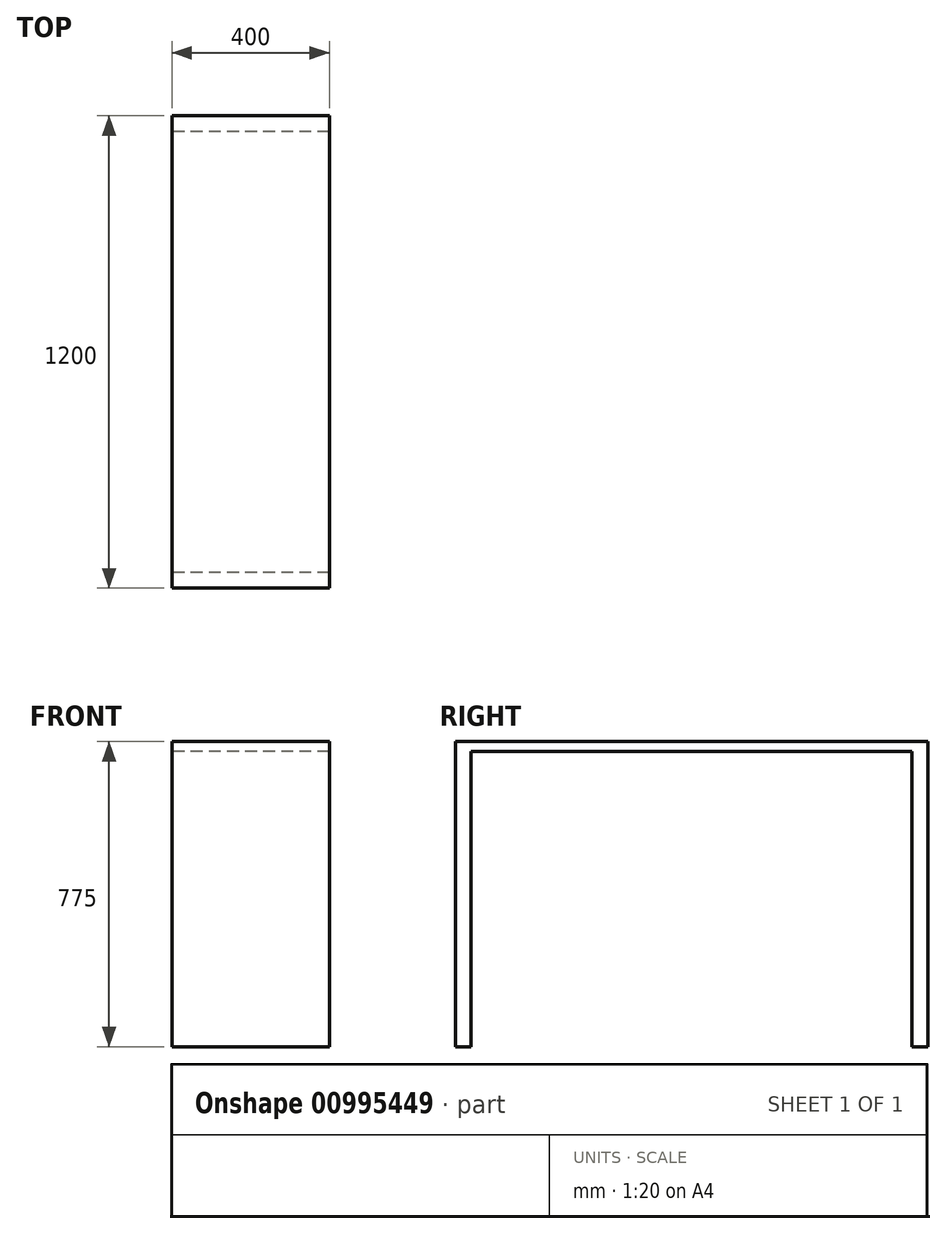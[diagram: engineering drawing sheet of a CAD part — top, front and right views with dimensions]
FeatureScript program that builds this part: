
annotation { "Feature Type Name" : "Feature", "Feature Type Description" : "" }
export const myFeature = defineFeature(function(context is Context, id is Id, definition is map)
    precondition{}
    {
        {
            var Q0;
            Q0=qCreatedBy(makeId("Top.planeOp"),FACE);
            var sketch = newSketch(context, id + "F0", { "sketchPlane" : qUnion([Q0])});
            skLineSegment(sketch, "E0.bottom", {"start": v(-183.76, 1047.63) * mm, "end": v(216.24, 1047.63) * mm});
            skLineSegment(sketch, "E0.top", {"start": v(-183.76, -152.37) * mm, "end": v(216.24, -152.37) * mm});
            skLineSegment(sketch, "E0.left", {"start": v(-183.76, 1047.63) * mm, "end": v(-183.76, -152.37) * mm});
            skLineSegment(sketch, "E0.right", {"start": v(216.24, 1047.63) * mm, "end": v(216.24, -152.37) * mm});
            skSolve(sketch);
        }
        {
            var Q0;
            Q0 = qSketchRegion(id + "F0", true);
            extrude(context, id + "F1", {"entities" : qUnion([Q0]), "depth" : 25 * mm, "offsetDistance" : 25 * mm});
        }
        {
            var Q0;
            Q0=makeQuery(id+"F1.opExtrude","CAP_FACE",FACE,{"disambiguationData":[OSD([sQuery(id+"F0.wireOp",EDGE,"E0.bottom"),sQuery(id+"F0.wireOp",EDGE,"E0.top"),sQuery(id+"F0.wireOp",EDGE,"E0.left"),sQuery(id+"F0.wireOp",EDGE,"E0.right")])],"isStart":true});
            var sketch = newSketch(context, id + "F2", { "sketchPlane" : qUnion([Q0])});
            skLineSegment(sketch, "E1", {"start": v(216.24, 112.37) * mm, "end": v(-183.76, 112.37) * mm});
            skLineSegment(sketch, "E2", {"start": v(216.24, -1007.63) * mm, "end": v(-183.76, -1007.63) * mm});
            skSolve(sketch);
        }
        {
            var Q0;
            {var subQ0=sQuery(id+"F2.wireOp",EDGE,"E2");Q0=makeQuery(id+"F2.imprint","IMPRINT",FACE,{"disambiguationData":[TD([[makeQuery(id+"F2.imprint","IMPRINT",EDGE,{"derivedFrom":subQ0}),1.0]])]});}
            var Q1;
            {var subQ0=sQuery(id+"F2.wireOp",EDGE,"E1");Q1=makeQuery(id+"F2.imprint","IMPRINT",FACE,{"disambiguationData":[TD([[makeQuery(id+"F2.imprint","IMPRINT",EDGE,{"derivedFrom":subQ0}),-1.0]])]});}
            extrude(context, id + "F3", {"entities" : qUnion([Q0, Q1]), "operationType" : NewBodyOperationType.ADD, "depth" : 750 * mm, "offsetDistance" : 25 * mm});
        }
    });
